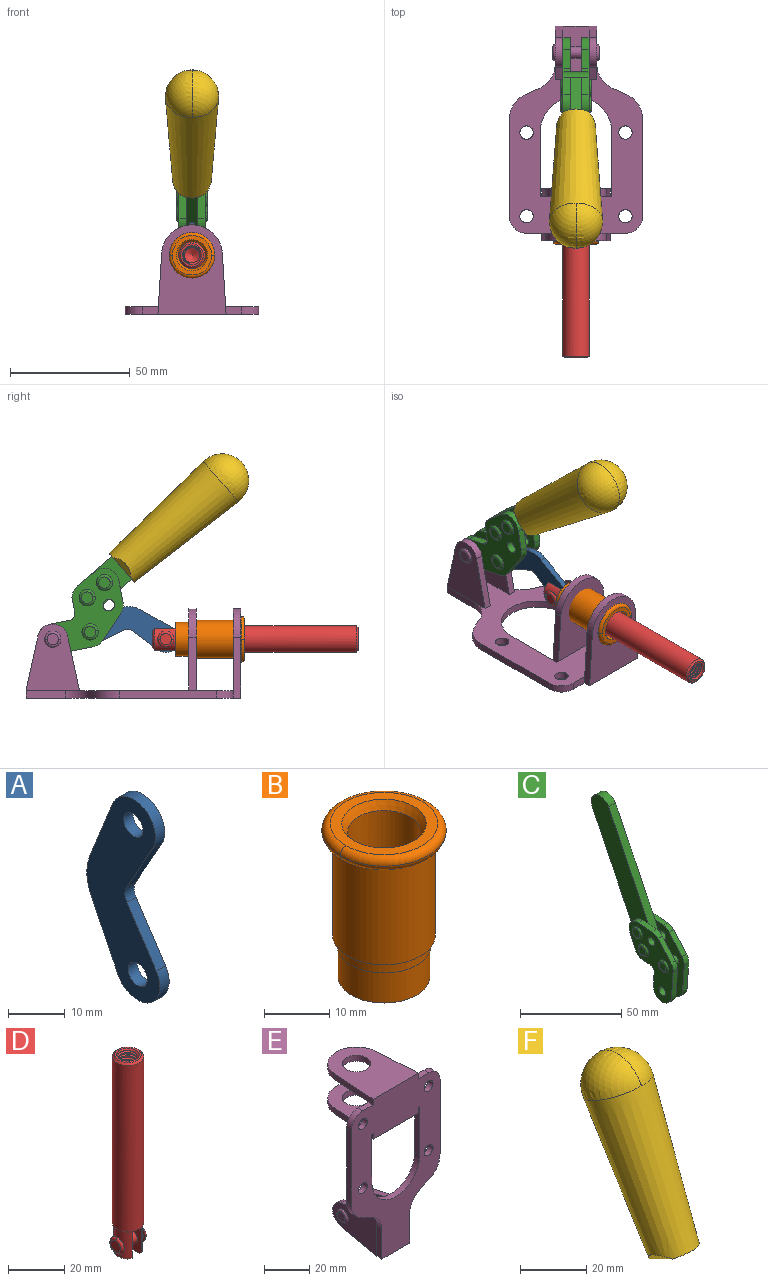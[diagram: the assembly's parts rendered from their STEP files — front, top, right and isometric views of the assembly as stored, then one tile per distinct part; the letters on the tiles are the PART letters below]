
ASSEMBLY  parts=6 mates=6
PART A: 12 faces, bbox 2.3x18.2x42.8 mm
  f0: cylinder r=2.4mm len=4.8mm, axis (1,0,0), area 34.9mm2, adj f4,f11
  f1: cylinder r=10.41mm len=8.47mm, axis (1,0,0), area 20.2mm2, adj f4,f9,f10,f11
  f2: cylinder r=3.05mm len=3.16mm, axis (1,0,0), area 7.7mm2, adj f4,f6,f7,f11
  f3: cylinder r=2.4mm len=4.8mm, axis (1,0,0), area 34.9mm2, adj f4,f11
  f4: plane 42.81x18.23mm, normal (-1,0,0), area 414.1mm2, adj f0,f1,f2,f3,f5,f6,f7,f8
  f5: cylinder r=5.54mm len=10.67mm, axis (1,0,0), area 41.8mm2, adj f4,f6,f10,f11
  f6: plane 11.66x6.53mm, normal (0,-0.87,-0.49), area 30.9mm2, adj f2,f4,f5,f11
  f7: plane 11.17x7.33mm, normal (0,-0.84,0.55), area 30.9mm2, adj f2,f4,f8,f11
  f8: cylinder r=5.54mm len=10.51mm, axis (1,0,0), area 41.8mm2, adj f4,f7,f9,f11
  f9: plane 13.67x6.67mm, normal (0,0.9,-0.44), area 35.1mm2, adj f1,f4,f8,f11
  f10: plane 14.1x5.7mm, normal (0,0.93,0.37), area 35.1mm2, adj f1,f4,f5,f11
  f11: plane 42.81x18.23mm, normal (1,0,0), area 414.1mm2, adj f0,f1,f2,f3,f5,f6,f7,f8
PART B: 15 faces, bbox 20.6x20.6x28.7 mm
  f0: torus R=8.26mm, axis (0,0,1), area 56.8mm2, adj f1,f10,f12
  f1: torus R=8.26mm, axis (0,0,1), area 56.8mm2, adj f0,f6,f13
  f2: cylinder r=5.59mm len=25.91mm, axis (0,0,1), area 909.6mm2, adj f3,f4
  f3: cone r=6.86mm half-angle=45deg, axis (0,0,-1), area 70.2mm2, adj f2,f14
  f4: cone r=6.47mm half-angle=30deg, axis (0,0,1), area 66.7mm2, adj f2,f13
  f5: cylinder r=7.04mm len=14.07mm, axis (0,0,1), area 252.6mm2, adj f11,f14
  f6: torus R=8.26mm, axis (0,0,1), area 56.8mm2, adj f1,f12,f13
  f7: cylinder r=7.16mm len=14.33mm, axis (0,0,1), area 91.5mm2, adj f9,f11
  f8: cylinder r=7.86mm len=18.42mm, axis (0,0,1), area 909.6mm2, adj f9,f10
  f9: plane 15.72x15.72mm, normal (0,0,-1), area 33mm2, adj f7,f8
  f10: plane 16.51x16.51mm, normal (0,0,-1), area 19.9mm2, adj f0,f8,f12
  f11: plane 14.33x14.33mm, normal (0,0,-1), area 5.7mm2, adj f5,f7
  f12: torus R=8.26mm, axis (0,0,1), area 56.8mm2, adj f0,f6,f10
  f13: plane 16.51x16.51mm, normal (0,0,1), area 82.7mm2, adj f1,f4,f6
  f14: plane 14.07x14.07mm, normal (0,0,-1), area 7.8mm2, adj f3,f5
PART C: 59 faces, bbox 12.9x60.2x99.6 mm
  f0: torus R=2.39mm, axis (-1,0,0), area 14.9mm2, adj f20,f43,f51
  f1: torus R=2.39mm, axis (-1,0,0), area 14.9mm2, adj f19,f42,f51
  f2: torus R=2.39mm, axis (-1,0,0), area 14.9mm2, adj f18,f35,f51
  f3: torus R=2.39mm, axis (-1,0,0), area 14.9mm2, adj f14,f17,f23
  f4: torus R=2.39mm, axis (-1,0,0), area 14.9mm2, adj f13,f16,f23
  f5: torus R=2.39mm, axis (-1,0,0), area 14.9mm2, adj f12,f15,f23
  f6: cylinder r=2.39mm len=4.78mm, axis (1,0,0), area 46.5mm2, adj f48,f50,f51
  f7: cylinder r=2.39mm len=4.78mm, axis (1,0,0), area 46.5mm2, adj f50,f51
  f8: cylinder r=6.35mm len=12.68mm, axis (1,0,0), area 61.8mm2, adj f38,f39,f50,f51
  f9: cylinder r=2.39mm len=4.78mm, axis (-1,0,0), area 70.5mm2, adj f46,f50
  f10: cylinder r=2.39mm len=4.78mm, axis (-1,0,0), area 46.5mm2, adj f23,f45,f46
  f11: cylinder r=2.39mm len=4.78mm, axis (-1,0,0), area 46.5mm2, adj f23,f46
  f12: plane 4.78x4.78mm, normal (1,0,0), area 17.9mm2, adj f5,f15
  f13: plane 4.78x4.78mm, normal (1,0,0), area 17.9mm2, adj f4,f16
  f14: plane 4.78x4.78mm, normal (1,0,0), area 17.9mm2, adj f3,f17
  f15: torus R=2.39mm, axis (-1,0,0), area 14.9mm2, adj f5,f12,f23
  f16: torus R=2.39mm, axis (-1,0,0), area 14.9mm2, adj f4,f13,f23
  f17: torus R=2.39mm, axis (-1,0,0), area 14.9mm2, adj f3,f14,f23
  f18: plane 4.78x4.78mm, normal (-1,0,0), area 17.9mm2, adj f2,f35
  f19: plane 4.78x4.78mm, normal (-1,0,0), area 17.9mm2, adj f1,f42
  f20: plane 4.78x4.78mm, normal (-1,0,0), area 17.9mm2, adj f0,f43
  f21: plane 2.26x0.2mm, normal (1,0,0), area 0.2mm2, adj f31,f44
  f22: plane 2.26x0.2mm, normal (-1,0,0), area 0.2mm2, adj f41,f44
  f23: plane 39.37x30.77mm, normal (1,0,0), area 565.5mm2, adj f3,f4,f5,f10,f11,f15,f16,f17
  f24: cylinder r=6.1mm len=4.15mm, axis (-1,0,0), area 14.7mm2, adj f23,f25,f32,f46
  f25: plane 10.25x9.01mm, normal (0,-0.75,0.66), area 42.3mm2, adj f23,f24,f26,f46
  f26: cylinder r=6.35mm len=4.64mm, axis (-1,0,0), area 15.6mm2, adj f23,f25,f27,f46
  f27: plane 15.84x3.1mm, normal (0,-1,-0.07), area 49.2mm2, adj f23,f26,f28,f46
  f28: cylinder r=6.35mm len=12.68mm, axis (-1,0,0), area 61.8mm2, adj f23,f27,f29,f46
  f29: plane 8.11x3.1mm, normal (0,1,0.07), area 25.2mm2, adj f23,f28,f30,f46
  f30: cylinder r=3.05mm len=3.25mm, axis (-1,0,0), area 14.8mm2, adj f23,f29,f31,f46
  f31: plane 5.99x3.1mm, normal (0,0.07,-1), area 18.6mm2, adj f21,f23,f30,f44,f46
  f32: plane 9.5x3.1mm, normal (0,-0.07,1), area 29.5mm2, adj f23,f24,f33,f46,f47
  f33: cylinder r=6.1mm len=8.63mm, axis (-1,0,0), area 39.1mm2, adj f23,f32,f34,f47
  f34: plane 8.65x3.96mm, normal (0,0.91,-0.42), area 29.5mm2, adj f23,f33,f44,f47
  f35: torus R=2.39mm, axis (-1,0,0), area 14.9mm2, adj f2,f18,f51
  f36: plane 10.25x9.01mm, normal (0,-0.75,0.66), area 42.3mm2, adj f37,f49,f50,f51
  f37: cylinder r=6.35mm len=4.64mm, axis (1,0,0), area 15.6mm2, adj f36,f38,f50,f51
  f38: plane 15.84x3.1mm, normal (0,-1,-0.07), area 49.2mm2, adj f8,f37,f50,f51
  f39: plane 8.11x3.1mm, normal (0,1,0.07), area 25.2mm2, adj f8,f40,f50,f51
  f40: cylinder r=3.05mm len=3.25mm, axis (1,0,0), area 14.8mm2, adj f39,f41,f50,f51
  f41: plane 5.99x3.1mm, normal (0,0.07,-1), area 18.6mm2, adj f22,f40,f44,f50,f51
  f42: torus R=2.39mm, axis (-1,0,0), area 14.9mm2, adj f1,f19,f51
  f43: torus R=2.39mm, axis (-1,0,0), area 14.9mm2, adj f0,f20,f51
  f44: cylinder r=6.35mm len=12.12mm, axis (-1,0,0), area 128.9mm2, adj f21,f22,f23,f31,f34,f41,f46,f47
  f45: plane 2.65x1.35mm, normal (1,0,0), area 1mm2, adj f10,f55
  f46: plane 39.08x20.42mm, normal (-1,0,0), area 412.5mm2, adj f9,f10,f11,f24,f25,f26,f27,f28
  f47: plane 77.62x39.82mm, normal (1,0,0), area 850mm2, adj f32,f33,f34,f44,f53,f54,f55
  f48: plane 2.65x1.35mm, normal (-1,0,0), area 1mm2, adj f6,f55
  f49: cylinder r=6.1mm len=4.15mm, axis (1,0,0), area 14.7mm2, adj f36,f50,f51,f56
  f50: plane 39.08x20.42mm, normal (1,0,0), area 412.5mm2, adj f6,f7,f8,f9,f36,f37,f38,f39
  f51: plane 39.37x30.77mm, normal (-1,0,0), area 565.5mm2, adj f0,f1,f2,f6,f7,f8,f35,f36
  f52: plane 8.65x3.96mm, normal (0,0.91,-0.42), area 29.5mm2, adj f44,f51,f57,f58
  f53: plane 68.49x33.4mm, normal (0,0.9,-0.44), area 358.1mm2, adj f44,f47,f54,f58
  f54: cylinder r=6.35mm len=12.06mm, axis (1,0,0), area 93.7mm2, adj f47,f53,f55,f58
  f55: plane 68.49x33.4mm, normal (0,-0.9,0.44), area 358.1mm2, adj f44,f45,f46,f47,f48,f50,f54,f58
  f56: plane 9.5x3.1mm, normal (0,-0.07,1), area 29.5mm2, adj f49,f50,f51,f57,f58
  f57: cylinder r=6.1mm len=8.63mm, axis (1,0,0), area 39.1mm2, adj f51,f52,f56,f58
  f58: plane 77.62x39.82mm, normal (-1,0,0), area 850mm2, adj f44,f52,f53,f54,f55,f56,f57
PART D: 48 faces, bbox 12.6x11.1x86.1 mm
  f0: torus R=2.41mm, axis (-1,0,0), area 15mm2, adj f30,f32,f34
  f1: torus R=2.41mm, axis (-1,0,0), area 15mm2, adj f29,f31,f33
  f2: cylinder r=5.54mm len=72.39mm, axis (0,0,1), area 2518.5mm2, adj f3,f4,f42,f43
  f3: cone r=5.54mm half-angle=45deg, axis (0,0,1), area 7.6mm2, adj f2,f5,f41
  f4: cone r=5.54mm half-angle=45deg, axis (0,0,-1), area 34.9mm2, adj f2,f39
  f5: cylinder r=5.08mm len=11.48mm, axis (0,0,1), area 108.3mm2, adj f3,f7,f8,f41
  f6: cylinder r=2.41mm len=4.83mm, axis (-1,0,0), area 71.2mm2, adj f40,f41
  f7: cylinder r=2.41mm len=4.83mm, axis (-1,0,0), area 7.6mm2, adj f5,f34
  f8: cone r=5.08mm half-angle=45deg, axis (0,0,1), area 10.6mm2, adj f5,f37,f41
  f9: cone r=3.98mm half-angle=45deg, axis (0,0,1), area 17.6mm2, adj f27,f39,f45,f46,f47
  f10: cylinder r=2.41mm len=4.83mm, axis (-1,0,0), area 7.6mm2, adj f33,f38
  f11: cylinder r=3.2mm len=6.4mm, axis (0,0,1), area 78.4mm2, adj f12,f28,f44,f45,f47
  f12: cylinder r=3.2mm len=6.4mm, axis (0,0,1), area 10.5mm2, adj f11,f13,f45,f47
  f13: cylinder r=3.2mm len=6.4mm, axis (0,0,1), area 10.5mm2, adj f12,f14,f45,f47
  f14: cylinder r=3.2mm len=6.4mm, axis (0,0,1), area 10.5mm2, adj f13,f15,f45,f47
  f15: cylinder r=3.2mm len=6.4mm, axis (0,0,1), area 10.5mm2, adj f14,f16,f45,f47
  f16: cylinder r=3.2mm len=6.4mm, axis (0,0,1), area 10.5mm2, adj f15,f17,f45,f47
  f17: cylinder r=3.2mm len=6.4mm, axis (0,0,1), area 10.5mm2, adj f16,f18,f45,f47
  f18: cylinder r=3.2mm len=6.4mm, axis (0,0,1), area 10.5mm2, adj f17,f19,f45,f47
  f19: cylinder r=3.2mm len=6.4mm, axis (0,0,1), area 10.5mm2, adj f18,f20,f45,f47
  f20: cylinder r=3.2mm len=6.4mm, axis (0,0,1), area 10.5mm2, adj f19,f21,f45,f47
  f21: cylinder r=3.2mm len=6.4mm, axis (0,0,1), area 10.5mm2, adj f20,f22,f45,f47
  f22: cylinder r=3.2mm len=6.4mm, axis (0,0,1), area 10.5mm2, adj f21,f23,f45,f47
  f23: cylinder r=3.2mm len=6.4mm, axis (0,0,1), area 10.5mm2, adj f22,f24,f45,f47
  f24: cylinder r=3.2mm len=6.4mm, axis (0,0,1), area 10.5mm2, adj f23,f25,f45,f47
  f25: cylinder r=3.2mm len=6.4mm, axis (0,0,1), area 10.5mm2, adj f24,f26,f45,f47
  f26: cylinder r=3.2mm len=6.4mm, axis (0,0,1), area 10.5mm2, adj f25,f27,f45,f47
  f27: cylinder r=3.2mm len=6.4mm, axis (0,0,1), area 7.4mm2, adj f9,f26,f45,f47
  f28: cone r=3.2mm half-angle=60deg, axis (0,0,1), area 37.2mm2, adj f11
  f29: plane 4.83x4.83mm, normal (-1,0,0), area 18.3mm2, adj f1,f31
  f30: plane 4.83x4.83mm, normal (1,0,0), area 18.3mm2, adj f0,f32
  f31: torus R=2.41mm, axis (-1,0,0), area 15mm2, adj f1,f29,f33
  f32: torus R=2.41mm, axis (-1,0,0), area 15mm2, adj f0,f30,f34
  f33: plane 6.83x6.83mm, normal (1,0,0), area 18.3mm2, adj f1,f10,f31
  f34: plane 6.83x6.83mm, normal (-1,0,0), area 18.3mm2, adj f0,f7,f32
  f35: cone r=5.08mm half-angle=45deg, axis (0,0,1), area 10.6mm2, adj f36,f38,f40
  f36: plane 7.25x1.97mm, normal (0,0,-1), area 10mm2, adj f35,f40
  f37: plane 7.25x1.97mm, normal (0,0,-1), area 10mm2, adj f8,f41
  f38: cylinder r=5.08mm len=11.48mm, axis (0,0,1), area 108.3mm2, adj f10,f35,f40,f42
  f39: plane 9.55x9.55mm, normal (0,0,1), area 22mm2, adj f4,f9
  f40: plane 12.76x10.09mm, normal (1,0,0), area 95.7mm2, adj f6,f35,f36,f38,f42,f43
  f41: plane 12.76x10.09mm, normal (-1,0,0), area 95.7mm2, adj f3,f5,f6,f8,f37,f43
  f42: cone r=5.54mm half-angle=45deg, axis (0,0,1), area 7.6mm2, adj f2,f38,f40
  f43: plane 11.07x4.7mm, normal (0,0,-1), area 50.4mm2, adj f2,f40,f41
  f44: plane 0.89x0.62mm, normal (-1,0,0), area 0.3mm2, adj f11,f45,f46,f47
  f45: bspline ~24.8x7.63mm, area 266.6mm2, adj f9,f11,f12,f13,f14,f15,f16,f17
  f46: bspline ~24.87x7.63mm, area 73.6mm2, adj f9,f44,f45,f47
  f47: bspline ~24.98x7.63mm, area 272.5mm2, adj f9,f11,f12,f13,f14,f15,f16,f17
PART E: 55 faces, bbox 55.7x37.4x89.8 mm
  f0: torus R=2.41mm, axis (-1,0,0), area 15mm2, adj f11,f15,f25
  f1: torus R=2.41mm, axis (-1,0,0), area 15mm2, adj f10,f12,f22
  f2: cylinder r=2.78mm len=5.56mm, axis (0,-1,0), area 54.2mm2, adj f30,f54
  f3: cylinder r=14.99mm len=29.97mm, axis (0,-1,0), area 145.9mm2, adj f30,f49,f53,f54
  f4: cylinder r=2.78mm len=5.56mm, axis (0,-1,0), area 54.2mm2, adj f30,f54
  f5: cylinder r=2.78mm len=5.56mm, axis (0,-1,0), area 54.2mm2, adj f30,f54
  f6: cylinder r=2.78mm len=5.56mm, axis (0,-1,0), area 54.2mm2, adj f30,f54
  f7: cylinder r=6.35mm len=12.7mm, axis (0,0,1), area 123.6mm2, adj f27,f51
  f8: cylinder r=6.35mm len=12.7mm, axis (0,0,-1), area 124.7mm2, adj f21,f35
  f9: cylinder r=2.41mm len=11.18mm, axis (-1,0,0), area 169.4mm2, adj f16,f19
  f10: plane 4.83x4.83mm, normal (1,0,0), area 18.3mm2, adj f1,f12
  f11: plane 4.83x4.83mm, normal (-1,0,0), area 18.3mm2, adj f0,f15
  f12: torus R=2.41mm, axis (-1,0,0), area 15mm2, adj f1,f10,f22
  f13: cylinder r=6.35mm len=12.41mm, axis (1,0,0), area 53.4mm2, adj f18,f19,f22,f23
  f14: cylinder r=6.35mm len=12.41mm, axis (-1,0,0), area 53.4mm2, adj f16,f17,f24,f25
  f15: torus R=2.41mm, axis (-1,0,0), area 15mm2, adj f0,f11,f25
  f16: plane 27.86x22.35mm, normal (1,0,0), area 425.4mm2, adj f9,f14,f17,f24,f30
  f17: plane 22.86x4.97mm, normal (0,0.21,0.98), area 72.5mm2, adj f14,f16,f25,f30
  f18: plane 22.86x4.97mm, normal (0,0.21,0.98), area 72.5mm2, adj f13,f19,f22,f30
  f19: plane 27.86x22.35mm, normal (-1,0,0), area 425.4mm2, adj f9,f13,f18,f23,f30
  f20: cylinder r=12.7mm len=25.35mm, axis (0,0,-1), area 119.8mm2, adj f21,f34,f35,f36
  f21: plane 34.21x28.07mm, normal (0,0,-1), area 702.4mm2, adj f8,f20,f30,f34,f36
  f22: plane 27.96x22.45mm, normal (1,0,0), area 407.2mm2, adj f1,f12,f13,f18,f23,f30,f42,f43
  f23: plane 22.86x4.97mm, normal (0,0.21,-0.98), area 72.5mm2, adj f13,f19,f22,f44
  f24: plane 22.86x4.97mm, normal (0,0.21,-0.98), area 72.5mm2, adj f14,f16,f25,f44
  f25: plane 27.86x22.35mm, normal (-1,0,0), area 407.1mm2, adj f0,f14,f15,f17,f24,f30,f45,f46
  f26: plane 3.1x0.95mm, normal (0,0,-1), area 2.7mm2, adj f30,f49,f50,f54
  f27: plane 34.21x28.07mm, normal (0,0,1), area 702.4mm2, adj f7,f28,f30,f50,f52
  f28: cylinder r=12.7mm len=25.35mm, axis (0,0,1), area 118.8mm2, adj f27,f50,f51,f52
  f29: plane 3.1x0.95mm, normal (0,0,-1), area 2.7mm2, adj f30,f52,f53,f54
  f30: plane 86.54x55.63mm, normal (0,1,0), area 2362.9mm2, adj f2,f3,f4,f5,f6,f16,f17,f18
  f31: plane 40.56x3.1mm, normal (-1,0,0), area 125.7mm2, adj f30,f32,f48,f54
  f32: cylinder r=7.11mm len=7.11mm, axis (0,-1,0), area 34.6mm2, adj f30,f31,f33,f54
  f33: plane 6.67x3.1mm, normal (0,0,1), area 20.4mm2, adj f30,f32,f34,f54
  f34: plane 25.39x3.13mm, normal (-1,0.06,0), area 79.5mm2, adj f20,f21,f33,f35,f54
  f35: plane 37.31x28.45mm, normal (0,0,1), area 789.9mm2, adj f8,f20,f34,f36,f54
  f36: plane 25.39x3.13mm, normal (1,0.06,0), area 79.5mm2, adj f20,f21,f35,f37,f54
  f37: plane 6.67x3.1mm, normal (0,0,1), area 20.4mm2, adj f30,f36,f38,f54
  f38: cylinder r=7.11mm len=7.11mm, axis (0,-1,0), area 34.6mm2, adj f30,f37,f39,f54
  f39: plane 40.56x3.1mm, normal (1,0,0), area 125.7mm2, adj f30,f38,f40,f54
  f40: cylinder r=11.18mm len=10.16mm, axis (0,-1,0), area 39.5mm2, adj f30,f39,f41,f54
  f41: plane 6.09x3.1mm, normal (0.42,0,-0.91), area 20.8mm2, adj f30,f40,f42,f54
  f42: cylinder r=11.18mm len=9.41mm, axis (0,-1,0), area 37.2mm2, adj f22,f30,f41,f43,f54
  f43: plane 16.5x3.1mm, normal (1,0,0), area 51.1mm2, adj f22,f42,f44,f54
  f44: plane 17.37x3.1mm, normal (0,0,-1), area 53.8mm2, adj f23,f24,f30,f43,f45,f54
  f45: plane 16.5x3.1mm, normal (-1,0,0), area 51.1mm2, adj f25,f44,f46,f54
  f46: cylinder r=11.18mm len=9.41mm, axis (0,-1,0), area 37.2mm2, adj f25,f30,f45,f47,f54
  f47: plane 6.09x3.1mm, normal (-0.42,0,-0.91), area 20.8mm2, adj f30,f46,f48,f54
  f48: cylinder r=11.18mm len=10.16mm, axis (0,-1,0), area 39.5mm2, adj f30,f31,f47,f54
  f49: plane 26.54x3.1mm, normal (-1,0,0), area 82.3mm2, adj f3,f26,f30,f54
  f50: plane 25.39x3.1mm, normal (1,0.06,0), area 78.8mm2, adj f26,f27,f28,f51,f54
  f51: plane 37.31x28.45mm, normal (0,0,-1), area 789.9mm2, adj f7,f28,f50,f52,f54
  f52: plane 25.39x3.1mm, normal (-1,0.06,0), area 78.8mm2, adj f27,f28,f29,f51,f54
  f53: plane 26.54x3.1mm, normal (1,0,0), area 82.3mm2, adj f3,f29,f30,f54
  f54: plane 89.66x55.63mm, normal (0,-1,0), area 2678.5mm2, adj f2,f3,f4,f5,f6,f26,f29,f31
PART F: 11 faces, bbox 22.3x42.6x64.5 mm
  f0: sphere r=11.13mm, area 411.4mm2, adj f1,f8
  f1: cone r=11.11mm half-angle=3.3deg, axis (0,0.44,0.9), area 3251.8mm2, adj f0,f7,f8,f9,f10
  f2: cylinder r=6.16mm len=11.7mm, axis (1,0,0), area 89.5mm2, adj f3,f4,f5,f6
  f3: plane 60.23x36.75mm, normal (-1,0,0), area 763.6mm2, adj f2,f4,f6,f10
  f4: plane 51.37x25.05mm, normal (0,0.9,-0.44), area 264.2mm2, adj f2,f3,f5,f10
  f5: plane 60.23x36.75mm, normal (1,0,0), area 763.6mm2, adj f2,f4,f6,f10
  f6: plane 51.37x25.05mm, normal (0,-0.9,0.44), area 264.2mm2, adj f2,f3,f5,f10
  f7: plane 9.95x5.95mm, normal (0.71,-0.31,-0.64), area 25.8mm2, adj f1,f10
  f8: sphere r=11.13mm, area 411.4mm2, adj f0,f1
  f9: plane 9.95x5.95mm, normal (-0.71,-0.31,-0.64), area 25.8mm2, adj f1,f10
  f10: plane 14.27x11.38mm, normal (0,-0.44,-0.9), area 106.7mm2, adj f1,f3,f4,f5,f6,f7,f9
PLACE A rot(axis=(1,0,0),97.5deg) t=(0,12.59,2.22)mm
PLACE B rot(axis=(1,0,0),90deg) t=(0,10.16,0)mm
PLACE C rot(axis=(1,0,0),75deg) t=(0,3.86,9.14)mm
PLACE D rot(axis=(1,0,0),90deg) t=(0,9.52,0)mm
PLACE E rot(axis=(1,0,0),90deg) t=(0,9.14,0)mm fixed
PLACE F rot(axis=(1,0,0),75deg) t=(0,3.86,9.14)mm
MATE revolute C.f4 <-> A.f3  axis (-1,0,0) through (0,25.65,27.64)mm
MATE revolute E.f0 <-> C.f7  axis (-1,0,0) through (0,41.23,24.61)mm
MATE fastened C.f54 <-> F.f2  axis (1,0,0) through (0,-30.66,91.94)mm
MATE slider D.f2 <-> E.f7  axis (0,-1,0) through (0,-49.26,24.61)mm
MATE revolute D.f6 <-> A.f5  axis (-1,0,0) through (0,-5.96,24.61)mm
MATE fastened B.f2 <-> E.f7  axis (0,1,0) through (0,-37.25,24.61)mm
